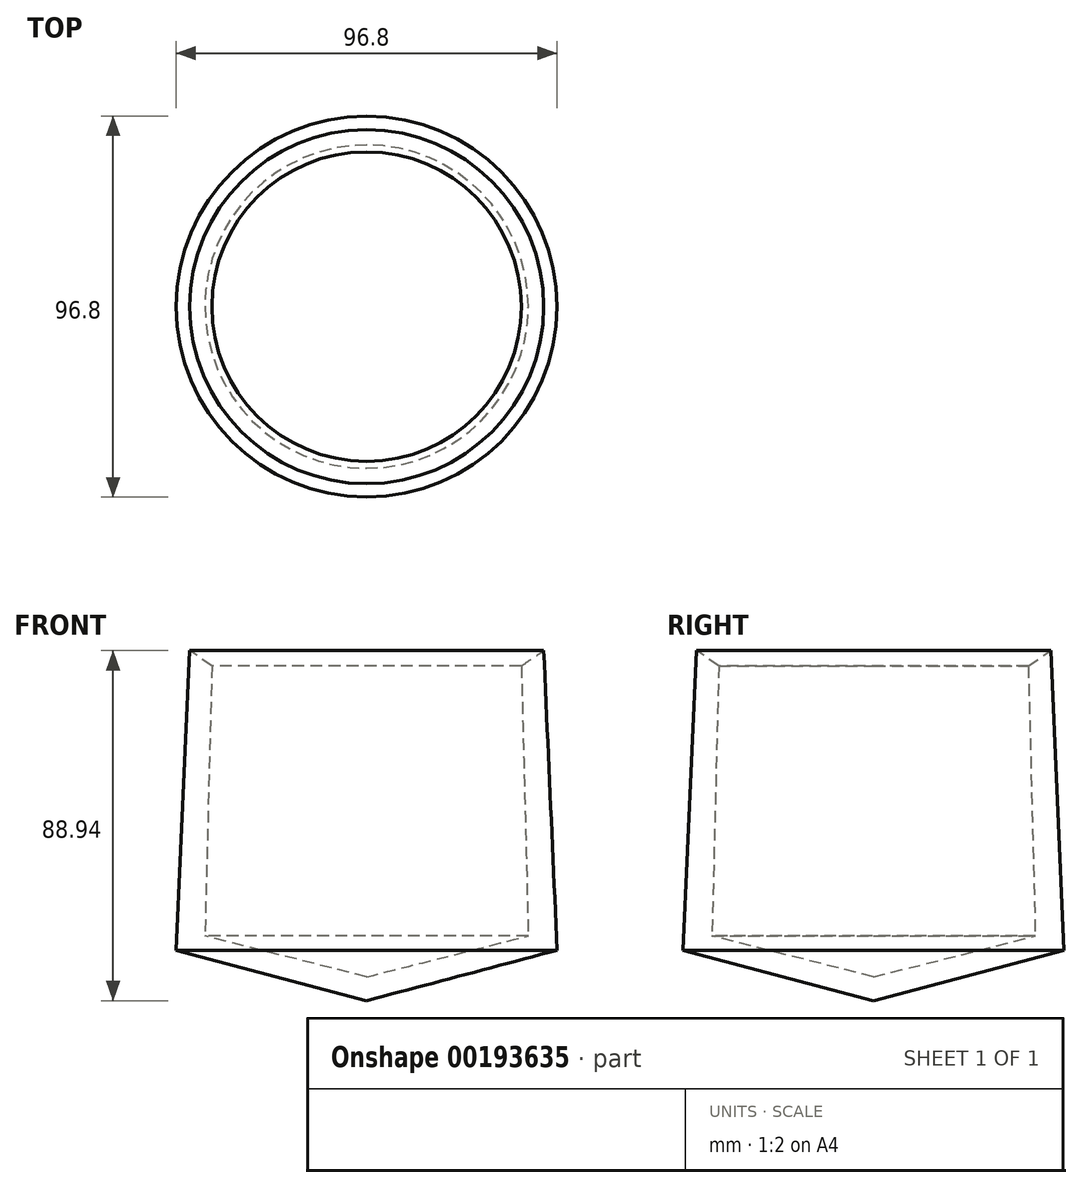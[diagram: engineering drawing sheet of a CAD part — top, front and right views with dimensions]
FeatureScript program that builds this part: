
annotation { "Feature Type Name" : "Feature", "Feature Type Description" : "" }
export const myFeature = defineFeature(function(context is Context, id is Id, definition is map)
    precondition{}
    {
        {
            var Q0;
            Q0=qCreatedBy(makeId("Front.planeOp"),FACE);
            var sketch = newSketch(context, id + "F0", { "sketchPlane" : qUnion([Q0])});
            skLineSegment(sketch, "E0", {"start": v(0, 43) * mm, "end": v(0, -45.9) * mm});
            skLineSegment(sketch, "E1", {"start": v(39.32, 39.13) * mm, "end": v(41.07, -29.43) * mm});
            skLineSegment(sketch, "E2", {"start": v(41.07, -29.43) * mm, "end": v(0, -39.9) * mm});
            skLineSegment(sketch, "E3", {"start": v(0, -39.9) * mm, "end": v(0, -45.9) * mm});
            skLineSegment(sketch, "E4", {"start": v(0, -45.9) * mm, "end": v(48.4, -33.1) * mm});
            skLineSegment(sketch, "E5", {"start": v(48.4, -33.1) * mm, "end": v(45, 43.03) * mm});
            skLineSegment(sketch, "E6", {"start": v(45, 43.03) * mm, "end": v(39.32, 39.13) * mm});
            skSolve(sketch);
        }
        {
            var Q0;
            Q0=makeQuery(id+"F0.imprint","IMPRINT",FACE,{"disambiguationData":[TD([[makeQuery(id+"F0.imprint","IMPRINT",EDGE,{"derivedFrom":sQuery(id+"F0.wireOp",EDGE,"E1")}),1.0]])]});
            var Q1;
            Q1=sQuery(id+"F0.wireOp",EDGE,"E0");
            revolve(context, id + "F1", {"entities" : qUnion([Q0]), "axis" : qUnion([Q1]), "revolveType" : RevolveType.FULL});
        }
    });
